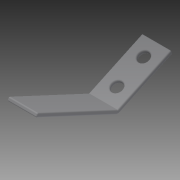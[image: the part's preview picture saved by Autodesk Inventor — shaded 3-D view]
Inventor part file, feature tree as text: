
AUTODESK INVENTOR PART (.ipt)
format: ipt  version: 2014 SP1 (Build 180222100, 222)  size: 147,968 bytes
history: native  units: in
note: dims shown in document units (in); Inventor stores cm internally (conversion verified against a paired STEP export)
features: sketch x3, extrude x2, other x1, fillet x1
ambient origin geometry x8: Origin, YZ Plane, XZ Plane, XY Plane, X Axis, Y Axis, Z Axis, Center Point
bodies: Solid1 (feature_tree)
feature tree (7):
  extrude  "Extrusion1"  Depth=0.5in
  extrude  "Extrusion2"  Depth=0.0625in
  other  "Bend Part1"
  fillet  "Fillet1"  Radius=0.25in
  sketch  "Sketch1"  dims[d0=0.5in d1=2.5in]
  sketch  "Sketch2"  dims[d2=0.0625in d3=0.0in d4=0.175in d5=0.25in]
  sketch  "Sketch3"  dims[d6=0.7874in d8=0.5in d9=0.3937in d11=1.0in d13=0.0625in d14=0.0in d15=0.25in d16=0.3436in d17=0.01in d18=0.02in]
